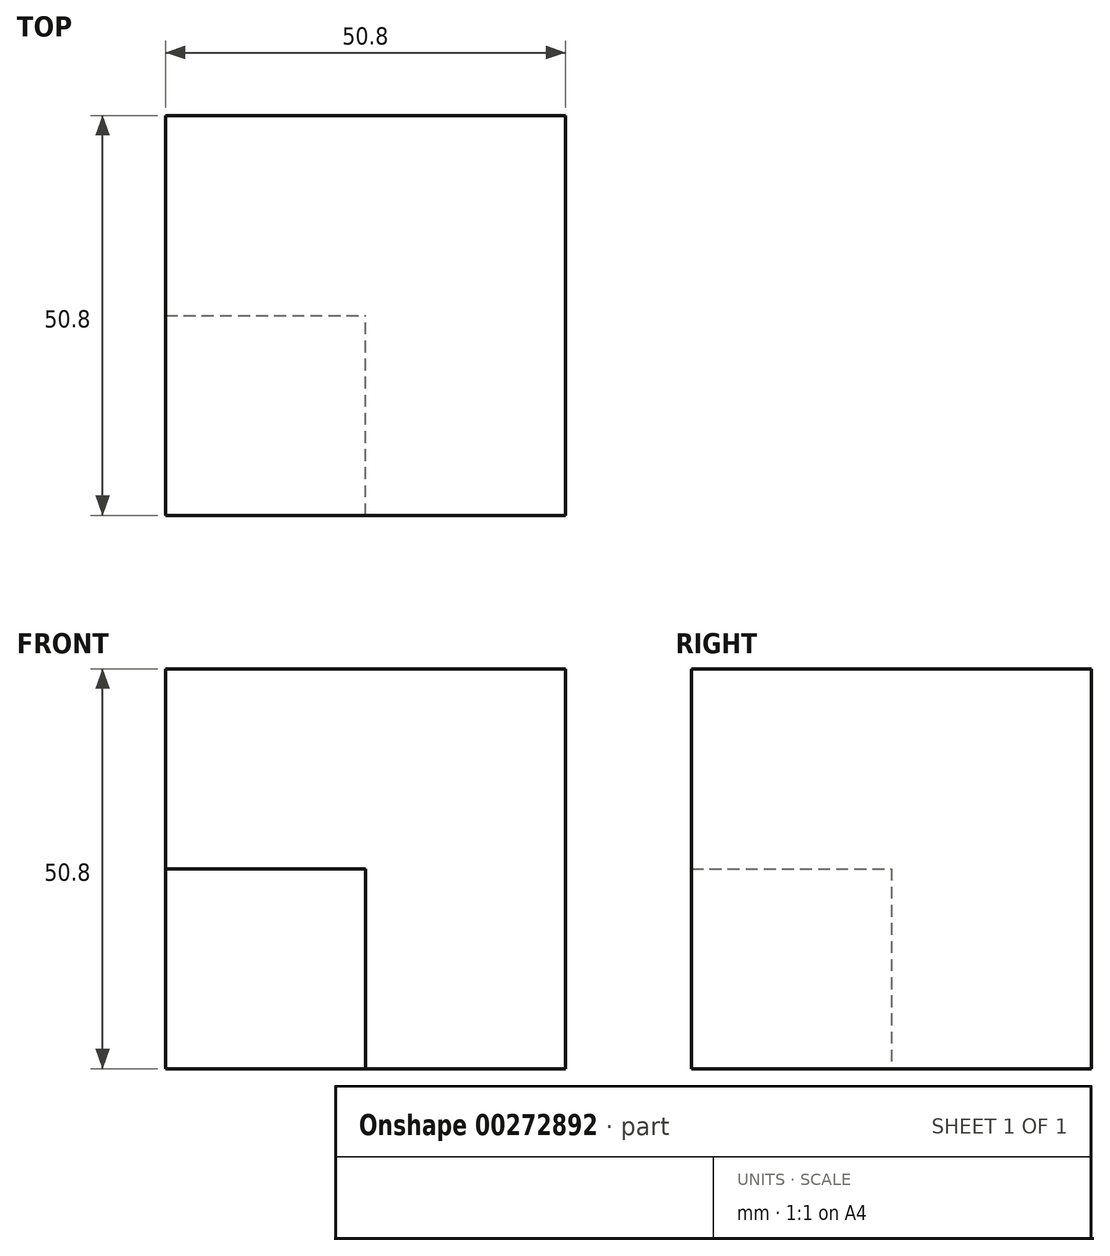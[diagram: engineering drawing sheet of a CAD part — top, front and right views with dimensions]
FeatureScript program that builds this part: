
annotation { "Feature Type Name" : "Feature", "Feature Type Description" : "" }
export const myFeature = defineFeature(function(context is Context, id is Id, definition is map)
    precondition{}
    {
        {
            var Q0;
            Q0=qCreatedBy(makeId("Front.planeOp"),FACE);
            var sketch = newSketch(context, id + "F0", { "sketchPlane" : qUnion([Q0])});
            skLineSegment(sketch, "E0", {"start": v(0, 0) * mm, "end": v(-50.8, 0) * mm});
            skLineSegment(sketch, "E1", {"start": v(-50.8, 50.8) * mm, "end": v(-50.8, 0) * mm});
            skPoint(sketch, "E2.end.orphan", {"position": v(0, 50.8) * mm});
            skLineSegment(sketch, "E3", {"start": v(-50.8, 50.8) * mm, "end": v(0, 50.8) * mm});
            skLineSegment(sketch, "E4", {"start": v(0, 0) * mm, "end": v(0, 50.8) * mm});
            skSolve(sketch);
        }
        {
            var Q0;
            Q0=makeQuery(id+"F0.imprint","IMPRINT",FACE,{"disambiguationData":[TD([[makeQuery(id+"F0.imprint","IMPRINT",EDGE,{"derivedFrom":sQuery(id+"F0.wireOp",EDGE,"E0")}),-1.0]])]});
            extrude(context, id + "F1", {"entities" : qUnion([Q0]), "depth" : 50.8 * mm});
        }
        {
            var Q0;
            Q0=makeQuery(id+"F1.opExtrude","SWEPT_FACE",FACE,{"disambiguationData":[OSD([sQuery(id+"F0.wireOp",EDGE,"E0")])]});
            var sketch = newSketch(context, id + "F2", { "sketchPlane" : qUnion([Q0])});
            skLineSegment(sketch, "E5.bottom", {"start": v(-50.8, 50.8) * mm, "end": v(-25.4, 50.8) * mm});
            skLineSegment(sketch, "E5.top", {"start": v(-50.8, 25.4) * mm, "end": v(-25.4, 25.4) * mm});
            skLineSegment(sketch, "E5.left", {"start": v(-50.8, 50.8) * mm, "end": v(-50.8, 25.4) * mm});
            skLineSegment(sketch, "E5.right", {"start": v(-25.4, 50.8) * mm, "end": v(-25.4, 25.4) * mm});
            skSolve(sketch);
        }
        {
            var Q0;
            Q0 = qSketchRegion(id + "F2", true);
            extrude(context, id + "F3", {"entities" : qUnion([Q0]), "operationType" : NewBodyOperationType.REMOVE, "oppositeDirection" : true, "depth" : 25.4 * mm});
        }
    });
